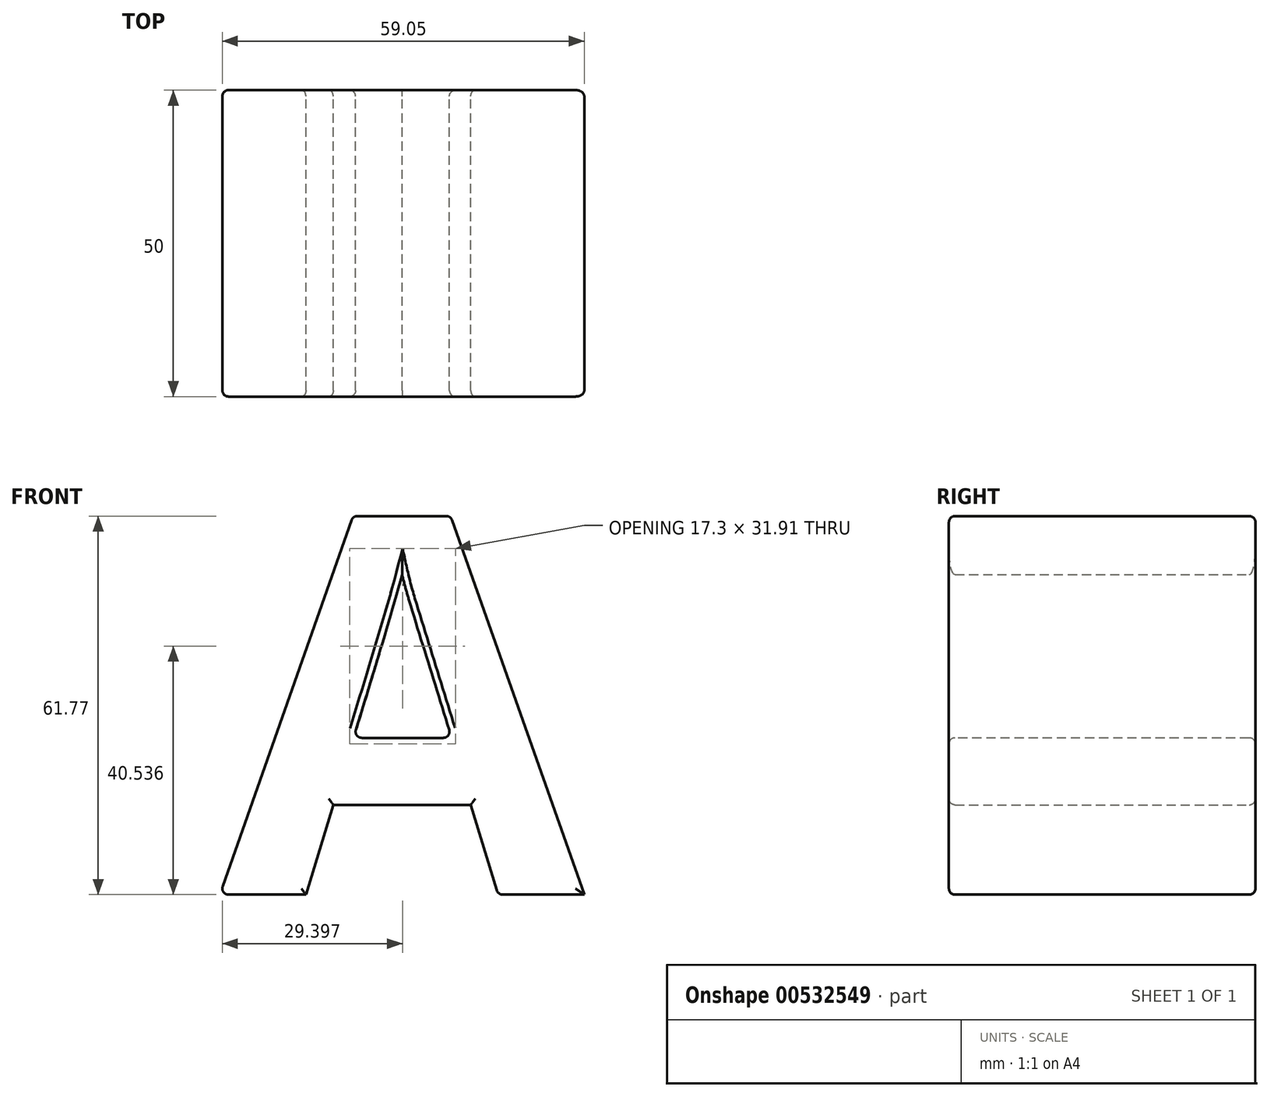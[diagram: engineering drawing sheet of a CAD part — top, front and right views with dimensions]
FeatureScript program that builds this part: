
annotation { "Feature Type Name" : "Feature", "Feature Type Description" : "" }
export const myFeature = defineFeature(function(context is Context, id is Id, definition is map)
    precondition{}
    {
        {
            var Q0;
            Q0=qCreatedBy(makeId("Front.planeOp"),FACE);
            var sketch = newSketch(context, id + "F0", { "sketchPlane" : qUnion([Q0])});
            skText(sketch, "E0", { "text": "A", "fontName": "OpenSans-Bold.ttf"});
            const initialGuessF0  = {"E0": [-0.03252, 0, 1, 0, 0.06204]};
            skSetInitialGuess(sketch, initialGuessF0);
            skSolve(sketch);
        }
        {
            var Q0;
            Q0 = qSketchRegion(id + "F0", true);
            extrude(context, id + "F1", {"entities" : qUnion([Q0]), "depth" : 50 * mm, "offsetDistance" : 25 * mm});
        }
        {
            var Q0;
            Q0=makeQuery(id+"F1.opExtrude","SWEPT_EDGE",EDGE,{"disambiguationData":[OSD([sQuery(id+"F0.wireOp",EDGE,"E0.sketch_text.stroke-4"),sQuery(id+"F0.wireOp",EDGE,"E0.sketch_text.stroke-5")])]});
            var Q1;
            Q1=makeQuery(id+"F1.opExtrude","CAP_EDGE",EDGE,{"disambiguationData":[OSD([sQuery(id+"F0.wireOp",EDGE,"E0.sketch_text.stroke-5")])],"isStart":true});
            var Q2;
            Q2=makeQuery(id+"F1.opExtrude","SWEPT_EDGE",EDGE,{"disambiguationData":[OSD([sQuery(id+"F0.wireOp",EDGE,"E0.sketch_text.stroke-5"),sQuery(id+"F0.wireOp",EDGE,"E0.sketch_text.stroke-6")])]});
            var Q3;
            Q3=makeQuery(id+"F1.opExtrude","CAP_EDGE",EDGE,{"disambiguationData":[OSD([sQuery(id+"F0.wireOp",EDGE,"E0.sketch_text.stroke-5")])],"isStart":false});
            var Q4;
            Q4=makeQuery(id+"F1.opExtrude","CAP_EDGE",EDGE,{"disambiguationData":[OSD([sQuery(id+"F0.wireOp",EDGE,"E0.sketch_text.stroke-6")])],"isStart":false});
            var Q5;
            Q5=makeQuery(id+"F1.opExtrude","CAP_EDGE",EDGE,{"disambiguationData":[OSD([sQuery(id+"F0.wireOp",EDGE,"E0.sketch_text.stroke-10")])],"isStart":false});
            var Q6;
            Q6=makeQuery(id+"F1.opExtrude","CAP_EDGE",EDGE,{"disambiguationData":[OSD([sQuery(id+"F0.wireOp",EDGE,"E0.sketch_text.stroke-8")])],"isStart":false});
            var Q7;
            Q7=makeQuery(id+"F1.opExtrude","CAP_EDGE",EDGE,{"disambiguationData":[OSD([sQuery(id+"F0.wireOp",EDGE,"E0.sketch_text.stroke-11")])],"isStart":false});
            var Q8;
            Q8=makeQuery(id+"F1.opExtrude","SWEPT_EDGE",EDGE,{"disambiguationData":[OSD([sQuery(id+"F0.wireOp",EDGE,"E0.sketch_text.stroke-8"),sQuery(id+"F0.wireOp",EDGE,"E0.sketch_text.stroke-11")])]});
            var Q9;
            Q9=makeQuery(id+"F1.opExtrude","CAP_EDGE",EDGE,{"disambiguationData":[OSD([sQuery(id+"F0.wireOp",EDGE,"E0.sketch_text.stroke-4")])],"isStart":false});
            var Q10;
            Q10=makeQuery(id+"F1.opExtrude","CAP_EDGE",EDGE,{"disambiguationData":[OSD([sQuery(id+"F0.wireOp",EDGE,"E0.sketch_text.stroke-1")])],"isStart":false});
            var Q11;
            Q11=makeQuery(id+"F1.opExtrude","SWEPT_EDGE",EDGE,{"disambiguationData":[OSD([sQuery(id+"F0.wireOp",EDGE,"E0.sketch_text.stroke-0"),sQuery(id+"F0.wireOp",EDGE,"E0.sketch_text.stroke-7")])]});
            var Q12;
            Q12=makeQuery(id+"F1.opExtrude","CAP_EDGE",EDGE,{"disambiguationData":[OSD([sQuery(id+"F0.wireOp",EDGE,"E0.sketch_text.stroke-2")])],"isStart":false});
            var Q13;
            Q13=makeQuery(id+"F1.opExtrude","CAP_EDGE",EDGE,{"disambiguationData":[OSD([sQuery(id+"F0.wireOp",EDGE,"E0.sketch_text.stroke-3")])],"isStart":false});
            var Q14;
            Q14=makeQuery(id+"F1.opExtrude","CAP_EDGE",EDGE,{"disambiguationData":[OSD([sQuery(id+"F0.wireOp",EDGE,"E0.sketch_text.stroke-7")])],"isStart":false});
            var Q15;
            Q15=makeQuery(id+"F1.opExtrude","CAP_EDGE",EDGE,{"disambiguationData":[OSD([sQuery(id+"F0.wireOp",EDGE,"E0.sketch_text.stroke-0")])],"isStart":false});
            var Q16;
            Q16=makeQuery(id+"F1.opExtrude","CAP_EDGE",EDGE,{"disambiguationData":[OSD([sQuery(id+"F0.wireOp",EDGE,"E0.sketch_text.stroke-10")])],"isStart":true});
            var Q17;
            Q17=makeQuery(id+"F1.opExtrude","SWEPT_EDGE",EDGE,{"disambiguationData":[OSD([sQuery(id+"F0.wireOp",EDGE,"E0.sketch_text.stroke-10"),sQuery(id+"F0.wireOp",EDGE,"E0.sketch_text.stroke-11")])]});
            var Q18;
            Q18=makeQuery(id+"F1.opExtrude","CAP_EDGE",EDGE,{"disambiguationData":[OSD([sQuery(id+"F0.wireOp",EDGE,"E0.sketch_text.stroke-11")])],"isStart":true});
            var Q19;
            Q19=makeQuery(id+"F1.opExtrude","CAP_EDGE",EDGE,{"disambiguationData":[OSD([sQuery(id+"F0.wireOp",EDGE,"E0.sketch_text.stroke-4")])],"isStart":true});
            var Q20;
            Q20=makeQuery(id+"F1.opExtrude","CAP_EDGE",EDGE,{"disambiguationData":[OSD([sQuery(id+"F0.wireOp",EDGE,"E0.sketch_text.stroke-3")])],"isStart":true});
            var Q21;
            Q21=makeQuery(id+"F1.opExtrude","CAP_EDGE",EDGE,{"disambiguationData":[OSD([sQuery(id+"F0.wireOp",EDGE,"E0.sketch_text.stroke-2")])],"isStart":true});
            var Q22;
            Q22=makeQuery(id+"F1.opExtrude","CAP_EDGE",EDGE,{"disambiguationData":[OSD([sQuery(id+"F0.wireOp",EDGE,"E0.sketch_text.stroke-1")])],"isStart":true});
            var Q23;
            Q23=makeQuery(id+"F1.opExtrude","CAP_EDGE",EDGE,{"disambiguationData":[OSD([sQuery(id+"F0.wireOp",EDGE,"E0.sketch_text.stroke-6")])],"isStart":true});
            var Q24;
            Q24=makeQuery(id+"F1.opExtrude","CAP_EDGE",EDGE,{"disambiguationData":[OSD([sQuery(id+"F0.wireOp",EDGE,"E0.sketch_text.stroke-8")])],"isStart":true});
            var Q25;
            Q25=makeQuery(id+"F1.opExtrude","CAP_EDGE",EDGE,{"disambiguationData":[OSD([sQuery(id+"F0.wireOp",EDGE,"E0.sketch_text.stroke-7")])],"isStart":true});
            var Q26;
            Q26=makeQuery(id+"F1.opExtrude","CAP_EDGE",EDGE,{"disambiguationData":[OSD([sQuery(id+"F0.wireOp",EDGE,"E0.sketch_text.stroke-0")])],"isStart":true});
            var Q27;
            Q27=makeQuery(id+"F1.opExtrude","SWEPT_EDGE",EDGE,{"disambiguationData":[OSD([sQuery(id+"F0.wireOp",EDGE,"E0.sketch_text.stroke-3"),sQuery(id+"F0.wireOp",EDGE,"E0.sketch_text.stroke-4")])]});
            var Q28;
            Q28=makeQuery(id+"F1.opExtrude","CAP_EDGE",EDGE,{"disambiguationData":[OSD([sQuery(id+"F0.wireOp",EDGE,"E0.sketch_text.stroke-9")])],"isStart":false});
            var Q29;
            Q29=makeQuery(id+"F1.opExtrude","CAP_EDGE",EDGE,{"disambiguationData":[OSD([sQuery(id+"F0.wireOp",EDGE,"E0.sketch_text.stroke-9")])],"isStart":true});
            fillet(context, id + "F2", {"entities" : qUnion([Q0, Q1, Q2, Q3, Q4, Q5, Q6, Q7, Q8, Q9, Q10, Q11, Q12, Q13, Q14, Q15, Q16, Q17, Q18, Q19, Q20, Q21, Q22, Q23, Q24, Q25, Q26, Q27, Q28, Q29]), "radius" : 1 * mm, "tangentPropagation" : true, "allowEdgeOverflow" : false});
        }
    });
